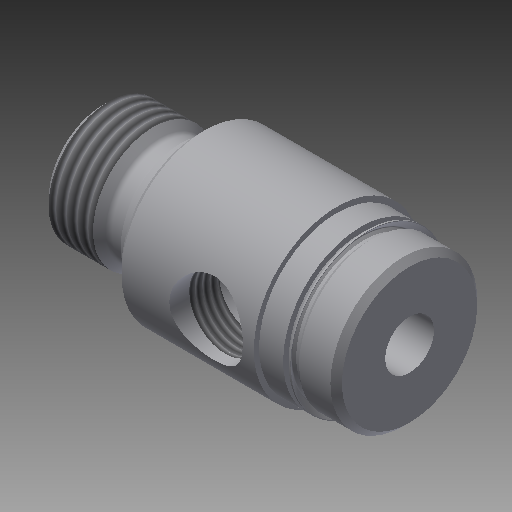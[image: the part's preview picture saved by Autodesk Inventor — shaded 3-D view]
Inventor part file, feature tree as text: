
AUTODESK INVENTOR PART (.ipt)
format: ipt  version: 2019.4 (Build 234330000, 330)  size: 325,632 bytes
history: native  units: in
note: dims shown in document units (in); Inventor stores cm internally (conversion verified against a paired STEP export)
features: other x119, sketch x6, revolve x5, thread x2, hole x1
ambient origin geometry x8: Origin, YZ Plane, XZ Plane, XY Plane, X Axis, Y Axis, Z Axis, Center Point
bodies: Solid1 (feature_tree)
feature tree (133):
  revolve  "Revolution1"  [1 undecoded]
  thread  "Thread1"  [1 undecoded]
  revolve  "Revolution2"  Angle=360.0deg
  hole  "Hole1"  [1 undecoded]
  revolve  "Revolution3"  [1 undecoded]
  revolve  "Revolution4"  [1 undecoded]
  thread  "Thread2"  [1 undecoded]
  revolve  "Revolution5"  [1 undecoded]
  other  "dp1_XY"
  other  "dp1_YZ"
  other  "dp1_ZX"
  other  "dp1_X"
  other  "dp1_Y"
  other  "dp1_Z"
  other  "dp1_Center"
  other  "dp2_XY"
  other  "dp2_YZ"
  other  "dp2_ZX"
  other  "dp2_X"
  other  "dp2_Y"
  other  "dp2_Z"
  other  "dp2_Center"
  other  "hh_XY"
  other  "hh_YZ"
  other  "hh_ZX"
  other  "hh_X"
  other  "hh_Y"
  other  "hh_Z"
  other  "hh_Center"
  other  "port_XY"
  other  "port_YZ"
  other  "port_ZX"
  other  "port_X"
  other  "port_Y"
  other  "port_Z"
  other  "port_Center"
  other  "rod_guide_XY"
  other  "rod_guide_YZ"
  other  "rod_guide_ZX"
  other  "rod_guide_X"
  other  "rod_guide_Y"
  other  "rod_guide_Z"
  other  "rod_guide_Center"
  other  "s1_XY"
  other  "s1_YZ"
  other  "s1_ZX"
  other  "s1_X"
  other  "s1_Y"
  other  "s1_Z"
  other  "s1_Center"
  other  "s2_XY"
  other  "s2_YZ"
  other  "s2_ZX"
  other  "s2_X"
  other  "s2_Y"
  other  "s2_Z"
  other  "s2_Center"
  other  "t1_XY"
  other  "t1_YZ"
  other  "t1_ZX"
  other  "t1_X"
  other  "t1_Y"
  other  "t1_Z"
  other  "t1_Center"
  other  "t111_XY"
  other  "t111_YZ"
  other  "t111_ZX"
  other  "t111_X"
  other  "t111_Y"
  other  "t111_Z"
  other  "t111_Center"
  other  "to_foot_bracket_XY"
  other  "to_foot_bracket_YZ"
  other  "to_foot_bracket_ZX"
  other  "to_foot_bracket_X"
  other  "to_foot_bracket_Y"
  other  "to_foot_bracket_Z"
  other  "to_foot_bracket_Center"
  other  "to_nut_XY"
  other  "to_nut_YZ"
  other  "to_nut_ZX"
  other  "to_nut_X"
  other  "to_nut_Y"
  other  "to_nut_Z"
  other  "to_nut_Center"
  other  "to_rod_XY"
  other  "to_rod_YZ"
  other  "to_rod_ZX"
  other  "to_rod_X"
  other  "to_rod_Y"
  other  "to_rod_Z"
  other  "to_rod_Center"
  other  "to_screw_XY"
  other  "to_screw_YZ"
  other  "to_screw_ZX"
  other  "to_screw_X"
  other  "to_screw_Y"
  other  "to_screw_Z"
  other  "to_screw_Center"
  other  "to_trunnion_brackets_XY"
  other  "to_trunnion_brackets_YZ"
  other  "to_trunnion_brackets_ZX"
  other  "to_trunnion_brackets_X"
  other  "to_trunnion_brackets_Y"
  other  "to_trunnion_brackets_Z"
  other  "to_trunnion_brackets_Center"
  other  "to_trunnion_brackets1_XY"
  other  "to_trunnion_brackets1_YZ"
  other  "to_trunnion_brackets1_ZX"
  other  "to_trunnion_brackets1_X"
  other  "to_trunnion_brackets1_Y"
  other  "to_trunnion_brackets1_Z"
  other  "to_trunnion_brackets1_Center"
  other  "to_trunnion_brackets2_XY"
  other  "to_trunnion_brackets2_YZ"
  other  "to_trunnion_brackets2_ZX"
  other  "to_trunnion_brackets2_X"
  other  "to_trunnion_brackets2_Y"
  other  "to_trunnion_brackets2_Z"
  other  "to_trunnion_brackets2_Center"
  other  "to_tube_XY"
  other  "to_tube_YZ"
  other  "to_tube_ZX"
  other  "to_tube_X"
  other  "to_tube_Y"
  other  "to_tube_Z"
  other  "to_tube_Center"
  sketch  "Sketch_2"  dims[d0=360.0deg d1=0.23in d2=0.0in d3=360.0deg]
  sketch  "Sketch_3"  dims[d4=0.2535in d5=0.75in d6=0.2735in d7=0.25in d8=90.0deg d9=1.594in d10=0.0in d11=360.0deg]
  sketch  "Sketch3"  dims[d12=360.0deg d13=0.1501in d14=0.0in]
  sketch  "Sketch_10"  dims[d15=360.0deg]
  sketch  "Sketch_40"  dims[d16=0.0in d17=0.0in d18=0.0in d19=0.0in d20=0.0in d21=0.0in]
  sketch  "Sketch_47"
note: 7 required parameter values undecoded (feature->parameter linkage not recoverable at this tier; creation-order binding heuristic only, values carry confidence <= 0.55)